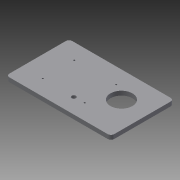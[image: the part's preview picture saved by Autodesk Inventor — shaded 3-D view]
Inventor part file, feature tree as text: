
AUTODESK INVENTOR PART (.ipt)
format: ipt  version: 2015 SP1 (Build 190203100, 203)  size: 348,672 bytes
history: native  units: mm
features: extrude x2, sketch x2, hole x1, pattern_linear x1, fillet x1
ambient origin geometry x8: Origin, YZ Plane, XZ Plane, XY Plane, X Axis, Y Axis, Z Axis, Center Point
bodies: Solid1 (feature_tree)
feature tree (7):
  extrude  "Extrusion1"  Depth=8.0mm
  extrude  "Extrusion2"  Depth=6.0mm
  hole  "Hole1"  [1 undecoded]
  pattern_linear  "Rectangular Pattern1"  Count1=7  [1 undecoded]
  fillet  "Fillet1"  Radius=150.0mm
  sketch  "Sketch1"  dims[d2=8.0mm d3=0.0mm d4=74.0mm]
  sketch  "Sketch2"  dims[d5=30.0mm d6=30.0mm d7=85.0mm d8=70.0mm d9=150.0mm d10=8.0mm d11=42.0mm d13=8.0mm d14=0.0mm d15=40.0mm d16=30.0mm d17=3.0mm d18=6.0mm d19=4.0mm d20=2.0mm d21=90.0deg d22=8.0mm d23=20.594885mm d24=20.0mm d26=80.0mm d27=20.0mm d29=60.0mm d30=6.0mm]
note: 2 required parameter values undecoded (feature->parameter linkage not recoverable at this tier; creation-order binding heuristic only, values carry confidence <= 0.55)
